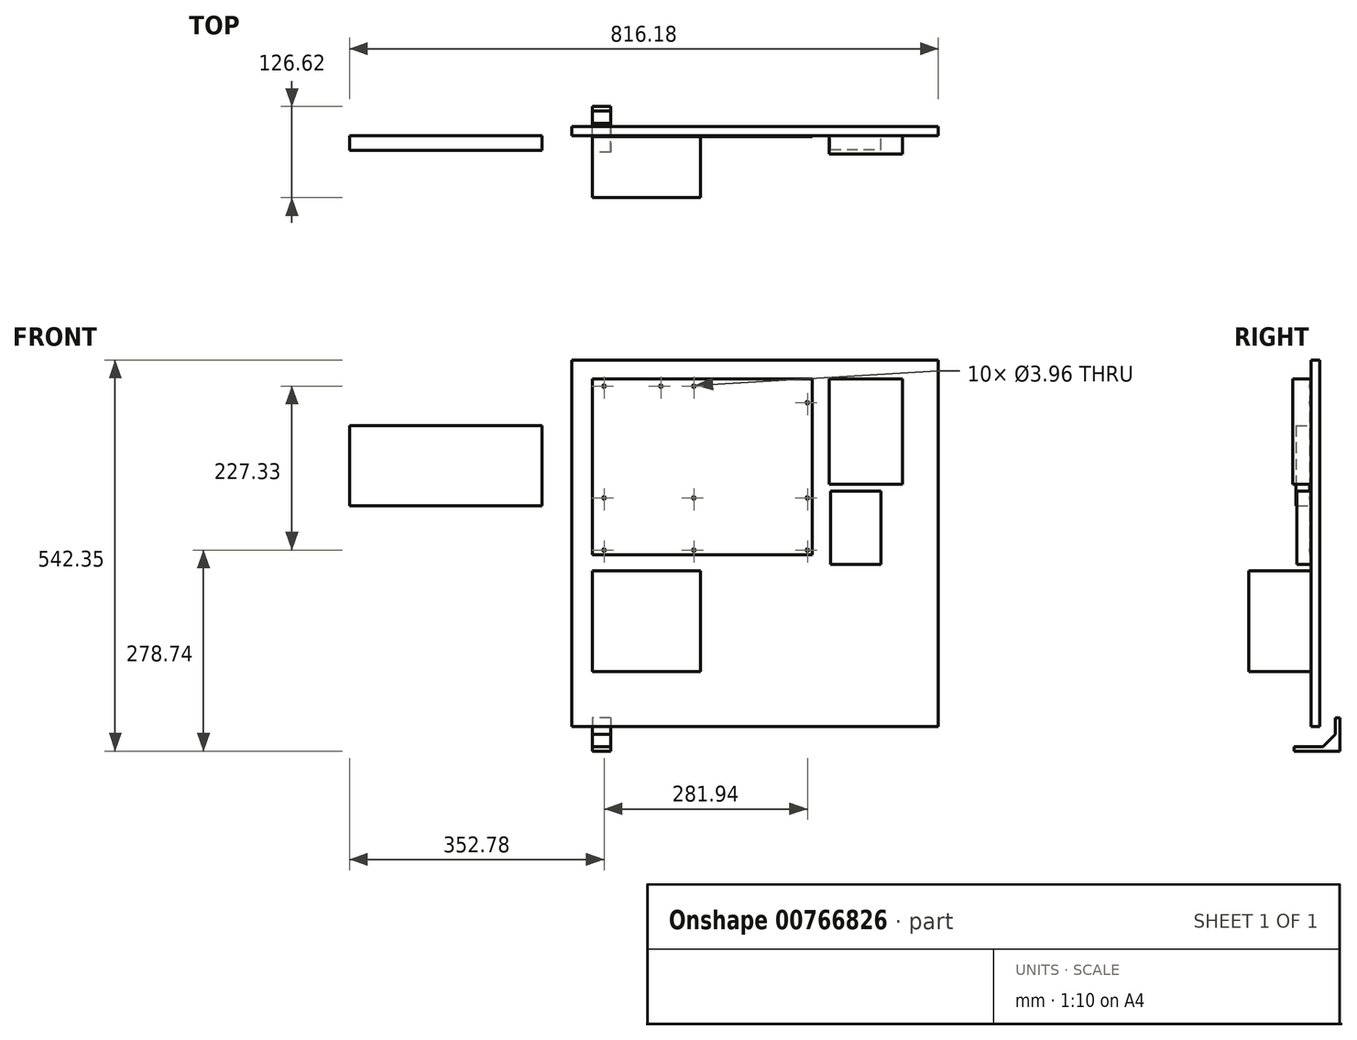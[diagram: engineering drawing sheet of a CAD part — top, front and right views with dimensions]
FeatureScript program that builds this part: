
annotation { "Feature Type Name" : "Feature", "Feature Type Description" : "" }
export const myFeature = defineFeature(function(context is Context, id is Id, definition is map)
    precondition{}
    {
        {
            var Q0;
            Q0=qCreatedBy(makeId("Front.planeOp"),FACE);
            var sketch = newSketch(context, id + "F0", { "sketchPlane" : qUnion([Q0])});
            skCircle(sketch, "E0", {"center": v(16.51, -10.16) * mm, "radius": 1.98 * mm});
            skCircle(sketch, "E1", {"center": v(140.97, -10.16) * mm, "radius": 1.98 * mm});
            skCircle(sketch, "E2", {"center": v(95.25, -10.16) * mm, "radius": 1.98 * mm});
            skCircle(sketch, "E3", {"center": v(298.45, -33.02) * mm, "radius": 1.98 * mm});
            skCircle(sketch, "E4", {"center": v(298.45, -165.1) * mm, "radius": 1.98 * mm});
            skCircle(sketch, "E5", {"center": v(298.45, -237.49) * mm, "radius": 1.98 * mm});
            skCircle(sketch, "E6", {"center": v(140.97, -165.1) * mm, "radius": 1.98 * mm});
            skCircle(sketch, "E7", {"center": v(140.97, -237.5) * mm, "radius": 1.98 * mm});
            skCircle(sketch, "E8", {"center": v(16.51, -165.1) * mm, "radius": 1.98 * mm});
            skCircle(sketch, "E9", {"center": v(16.51, -237.5) * mm, "radius": 1.98 * mm});
            skLineSegment(sketch, "E10.bottom", {"start": v(0, 0) * mm, "end": v(304.8, 0) * mm});
            skLineSegment(sketch, "E10.top", {"start": v(0, -243.84) * mm, "end": v(304.8, -243.84) * mm});
            skLineSegment(sketch, "E10.left", {"start": v(0, 0) * mm, "end": v(0, -243.84) * mm});
            skLineSegment(sketch, "E10.right", {"start": v(304.8, 0) * mm, "end": v(304.8, -243.84) * mm});
            skSolve(sketch);
        }
        {
            var Q0;
            Q0=qSketchRegion(id+"F0",true);
            extrude(context, id + "F1", {"entities" : qUnion([Q0]), "depth" : 1.57 * mm, "offsetDistance" : 25.4 * mm});
        }
        {
            var Q0;
            Q0=qCreatedBy(makeId("Front.planeOp"),FACE);
            var sketch = newSketch(context, id + "F2", { "sketchPlane" : qUnion([Q0])});
            skLineSegment(sketch, "E11.bottom", {"start": v(150, -406.22) * mm, "end": v(0, -406.22) * mm});
            skLineSegment(sketch, "E11.top", {"start": v(150, -266.22) * mm, "end": v(0, -266.22) * mm});
            skLineSegment(sketch, "E11.left", {"start": v(150, -406.22) * mm, "end": v(150, -266.22) * mm});
            skLineSegment(sketch, "E11.right", {"start": v(0, -406.22) * mm, "end": v(0, -266.22) * mm});
            skSolve(sketch);
        }
        {
            var Q0;
            Q0=qSketchRegion(id+"F2",true);
            extrude(context, id + "F3", {"entities" : qUnion([Q0]), "depth" : 86 * mm});
        }
        {
            var Q0;
            Q0=qCreatedBy(makeId("Front.planeOp"),FACE);
            var sketch = newSketch(context, id + "F4", { "sketchPlane" : qUnion([Q0])});
            skLineSegment(sketch, "E12.bottom", {"start": v(-69.57, -65.05) * mm, "end": v(-336.27, -65.05) * mm});
            skLineSegment(sketch, "E12.top", {"start": v(-69.57, -176.2) * mm, "end": v(-336.27, -176.2) * mm});
            skLineSegment(sketch, "E12.left", {"start": v(-69.57, -65.05) * mm, "end": v(-69.57, -176.2) * mm});
            skLineSegment(sketch, "E12.right", {"start": v(-336.27, -65.05) * mm, "end": v(-336.27, -176.2) * mm});
            skSolve(sketch);
        }
        {
            var Q0;
            Q0=qSketchRegion(id+"F4",true);
            extrude(context, id + "F5", {"entities" : qUnion([Q0]), "operationType" : NewBodyOperationType.ADD, "depth" : 20.32 * mm});
        }
        {
            var Q0;
            Q0=qCreatedBy(makeId("Front.planeOp"),FACE);
            var sketch = newSketch(context, id + "F6", { "sketchPlane" : qUnion([Q0])});
            skLineSegment(sketch, "E13.bottom", {"start": v(328.46, -146.05) * mm, "end": v(430.06, -146.05) * mm});
            skLineSegment(sketch, "E13.top", {"start": v(328.46, 0) * mm, "end": v(430.06, 0) * mm});
            skLineSegment(sketch, "E13.left", {"start": v(328.46, -146.05) * mm, "end": v(328.46, 0) * mm});
            skLineSegment(sketch, "E13.right", {"start": v(430.06, -146.05) * mm, "end": v(430.06, 0) * mm});
            skSolve(sketch);
        }
        {
            var Q0;
            Q0=qSketchRegion(id+"F6",true);
            extrude(context, id + "F7", {"entities" : qUnion([Q0]), "depth" : 25.4 * mm});
        }
        {
            var Q0;
            Q0=qCreatedBy(makeId("Front.planeOp"),FACE);
            var sketch = newSketch(context, id + "F8", { "sketchPlane" : qUnion([Q0])});
            skLineSegment(sketch, "E14.bottom", {"start": v(330.23, -257.37) * mm, "end": v(400.08, -257.37) * mm});
            skLineSegment(sketch, "E14.top", {"start": v(330.23, -155.77) * mm, "end": v(400.08, -155.77) * mm});
            skLineSegment(sketch, "E14.left", {"start": v(330.23, -257.37) * mm, "end": v(330.23, -155.77) * mm});
            skLineSegment(sketch, "E14.right", {"start": v(400.08, -257.37) * mm, "end": v(400.08, -155.77) * mm});
            skSolve(sketch);
        }
        {
            var Q0;
            Q0=qSketchRegion(id+"F8",true);
            extrude(context, id + "F9", {"entities" : qUnion([Q0]), "depth" : 19.05 * mm});
        }
        {
            var Q0;
            Q0=qCreatedBy(makeId("Front.planeOp"),FACE);
            var sketch = newSketch(context, id + "F10", { "sketchPlane" : qUnion([Q0])});
            skLineSegment(sketch, "E15.bottom", {"start": v(-28.09, 26.12) * mm, "end": v(479.91, 26.12) * mm});
            skLineSegment(sketch, "E15.top", {"start": v(-28.09, -481.88) * mm, "end": v(479.91, -481.88) * mm});
            skLineSegment(sketch, "E15.left", {"start": v(-28.09, 26.12) * mm, "end": v(-28.09, -481.88) * mm});
            skLineSegment(sketch, "E15.right", {"start": v(479.91, 26.12) * mm, "end": v(479.91, -481.88) * mm});
            skSolve(sketch);
        }
        {
            var Q0;
            Q0=makeQuery(id+"F10.imprint","IMPRINT",FACE,{"disambiguationData":[TD([[makeQuery(id+"F10.imprint","IMPRINT",EDGE,{"derivedFrom":sQuery(id+"F10.wireOp",EDGE,"E15.bottom")}),-1.0]])]});
            extrude(context, id + "F11", {"entities" : qUnion([Q0]), "oppositeDirection" : true, "depth" : 12.7 * mm});
        }
        {
            var Q0;
            Q0=qCreatedBy(makeId("Right.planeOp"),FACE);
            var sketch = newSketch(context, id + "F12", { "sketchPlane" : qUnion([Q0])});
            skLineSegment(sketch, "E16.bottom", {"start": v(34.27, -470.07) * mm, "end": v(40.62, -470.07) * mm});
            skLineSegment(sketch, "E16.left", {"start": v(34.27, -470.07) * mm, "end": v(34.27, -492.65) * mm});
            skLineSegment(sketch, "E16.right", {"start": v(40.62, -470.07) * mm, "end": v(40.62, -516.23) * mm});
            skLineSegment(sketch, "E17.top", {"start": v(17.04, -509.88) * mm, "end": v(-22.88, -509.88) * mm});
            skLineSegment(sketch, "E17.right", {"start": v(-22.88, -516.23) * mm, "end": v(-22.88, -509.88) * mm});
            skLineSegment(sketch, "E18", {"start": v(-22.88, -516.23) * mm, "end": v(40.62, -516.23) * mm});
            skLineSegment(sketch, "E19", {"start": v(17.04, -509.88) * mm, "end": v(34.27, -492.65) * mm});
            skSolve(sketch);
        }
        {
            var Q0;
            Q0=qSketchRegion(id+"F12",true);
            extrude(context, id + "F13", {"entities" : qUnion([Q0]), "depth" : 25.4 * mm});
        }
    });
